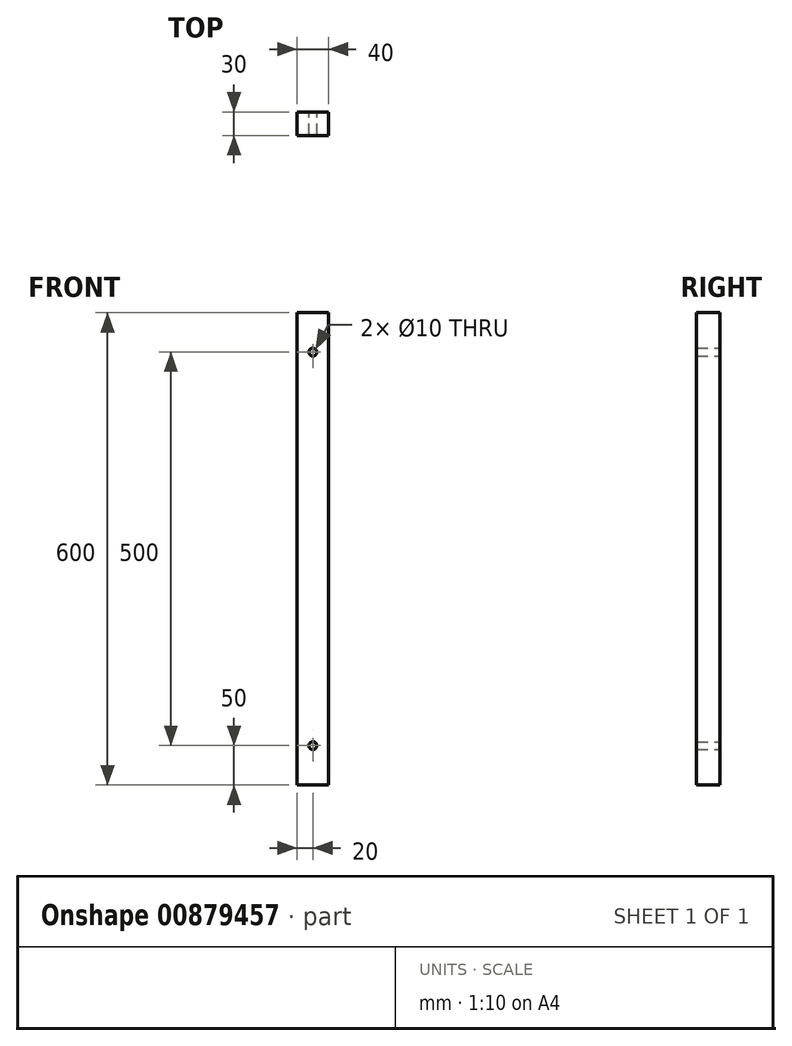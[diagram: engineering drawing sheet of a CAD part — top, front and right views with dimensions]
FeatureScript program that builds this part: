
annotation { "Feature Type Name" : "Feature", "Feature Type Description" : "" }
export const myFeature = defineFeature(function(context is Context, id is Id, definition is map)
    precondition{}
    {
        {
            var Q0;
            Q0=qCreatedBy(makeId("Front.planeOp"),FACE);
            var sketch = newSketch(context, id + "F0", { "sketchPlane" : qUnion([Q0])});
            skLineSegment(sketch, "E0.bottom", {"start": v(20, -300) * mm, "end": v(-20, -300) * mm});
            skLineSegment(sketch, "E0.top", {"start": v(20, 300) * mm, "end": v(-20, 300) * mm});
            skLineSegment(sketch, "E0.left", {"start": v(20, -300) * mm, "end": v(20, 300) * mm});
            skLineSegment(sketch, "E0.right", {"start": v(-20, -300) * mm, "end": v(-20, 300) * mm});
            skPoint(sketch, "E0.middle", {"position": v(0, 0) * mm});
            skCircle(sketch, "E1", {"center": v(0, 250) * mm, "radius": 5 * mm});
            skPoint(sketch, "E1.centerSnap0", {"position": v(0, 300) * mm});
            skLineSegment(sketch, "E2", {"start": v(-20, 0) * mm, "end": v(20, 0) * mm, "construction": true});
            skCircle(sketch, "E3.MirrorC", {"center": v(0, -250) * mm, "radius": 5 * mm});
            skSolve(sketch);
        }
        {
            var Q0;
            Q0=makeQuery(id+"F0.imprint","IMPRINT",FACE,{"disambiguationData":[TD([[makeQuery(id+"F0.imprint","IMPRINT",EDGE,{"derivedFrom":sQuery(id+"F0.wireOp",EDGE,"E0.bottom")}),-1.0]])]});
            extrude(context, id + "F1", {"entities" : qUnion([Q0]), "depth" : 30 * mm, "offsetDistance" : 25 * mm});
        }
    });
